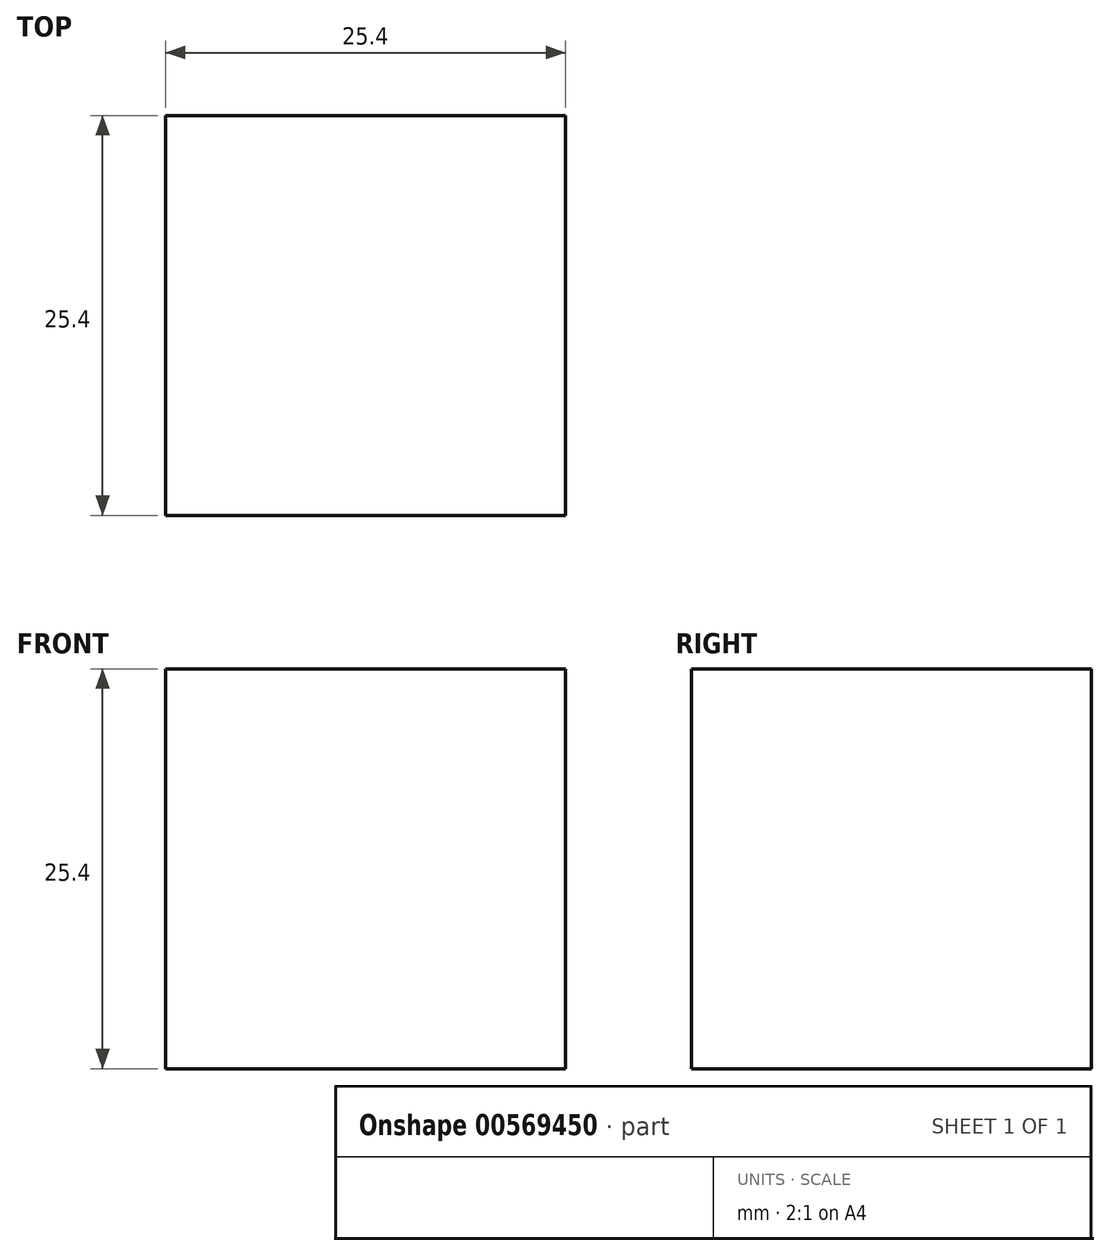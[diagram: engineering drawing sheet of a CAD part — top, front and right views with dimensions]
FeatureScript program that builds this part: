
annotation { "Feature Type Name" : "Feature", "Feature Type Description" : "" }
export const myFeature = defineFeature(function(context is Context, id is Id, definition is map)
    precondition{}
    {
        {
            var Q0;
            Q0=qCreatedBy(makeId("Front.planeOp"),FACE);
            var sketch = newSketch(context, id + "F0", { "sketchPlane" : qUnion([Q0])});
            skLineSegment(sketch, "E0.bottom", {"start": v(-25.4, 34.09) * mm, "end": v(0, 34.09) * mm});
            skLineSegment(sketch, "E0.top", {"start": v(-25.4, 8.69) * mm, "end": v(0, 8.69) * mm});
            skLineSegment(sketch, "E0.left", {"start": v(-25.4, 34.09) * mm, "end": v(-25.4, 8.69) * mm});
            skLineSegment(sketch, "E0.right", {"start": v(0, 34.09) * mm, "end": v(0, 8.69) * mm});
            skSolve(sketch);
        }
        {
            var Q0;
            Q0=makeQuery(id+"F0.imprint","IMPRINT",FACE,{"disambiguationData":[TD([[makeQuery(id+"F0.imprint","IMPRINT",EDGE,{"derivedFrom":sQuery(id+"F0.wireOp",EDGE,"E0.bottom")}),-1.0]])]});
            extrude(context, id + "F1", {"entities" : qUnion([Q0]), "depth" : 25.4 * mm, "offsetDistance" : 25.4 * mm});
        }
    });
